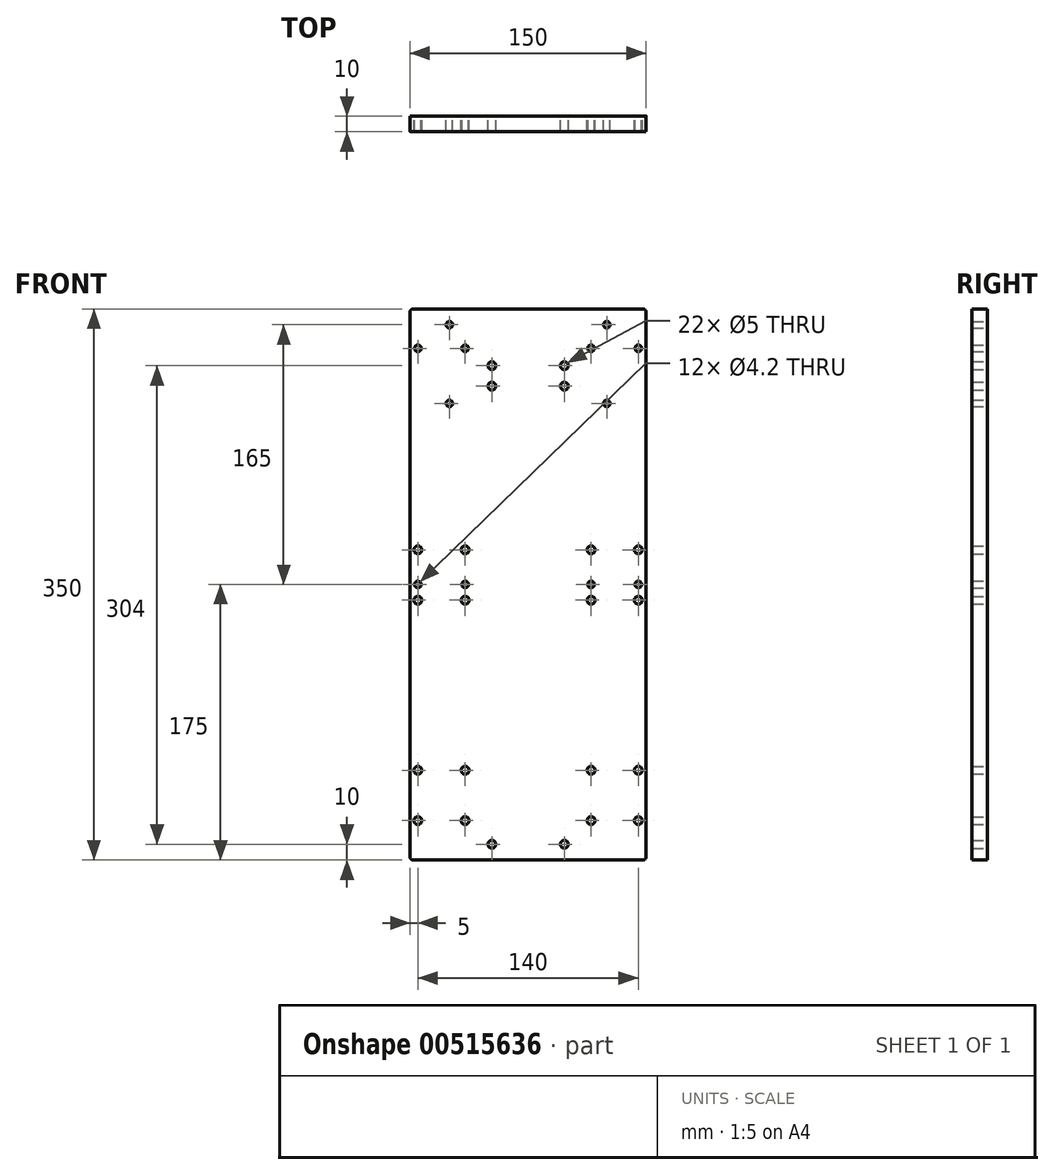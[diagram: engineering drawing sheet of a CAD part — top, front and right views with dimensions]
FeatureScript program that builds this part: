
annotation { "Feature Type Name" : "Feature", "Feature Type Description" : "" }
export const myFeature = defineFeature(function(context is Context, id is Id, definition is map)
    precondition{}
    {
        {
            var Q0;
            Q0=qCreatedBy(makeId("Front.planeOp"),FACE);
            var sketch = newSketch(context, id + "F0", { "sketchPlane" : qUnion([Q0]), "disableImprinting" : false});
            skLineSegment(sketch, "E0.bottom", {"start": v(-73, 175) * mm, "end": v(73, 175) * mm});
            skLineSegment(sketch, "E0.top", {"start": v(-73, -175) * mm, "end": v(73, -175) * mm});
            skLineSegment(sketch, "E0.left", {"start": v(-75, 173) * mm, "end": v(-75, -173) * mm});
            skLineSegment(sketch, "E0.right", {"start": v(75, 173) * mm, "end": v(75, -173) * mm});
            skPoint(sketch, "E0.middle", {"position": v(0, 0) * mm});
            skLineSegment(sketch, "E1", {"start": v(-55, 175) * mm, "end": v(-55, -175) * mm, "construction": true});
            skCircle(sketch, "E2", {"center": v(-70, 0) * mm, "radius": 2.1 * mm});
            skCircle(sketch, "E3.MirrorC", {"center": v(-40, 0) * mm, "radius": 2.1 * mm});
            skCircle(sketch, "E4.MirrorC", {"center": v(40, 0) * mm, "radius": 2.1 * mm});
            skCircle(sketch, "E5.MirrorC", {"center": v(70, 0) * mm, "radius": 2.1 * mm});
            skLineSegment(sketch, "E6", {"start": v(-75, -150) * mm, "end": v(75, -150) * mm, "construction": true});
            skCircle(sketch, "E7", {"center": v(-70, -150) * mm, "radius": 2.5 * mm});
            skCircle(sketch, "E8.MirrorC", {"center": v(-40, -150) * mm, "radius": 2.5 * mm});
            skCircle(sketch, "E9.MirrorC", {"center": v(40, -150) * mm, "radius": 2.5 * mm});
            skCircle(sketch, "E10.MirrorC", {"center": v(70, -150) * mm, "radius": 2.5 * mm});
            skLineSegment(sketch, "E11", {"start": v(-75, -134) * mm, "end": v(-55, -134) * mm, "construction": true});
            skCircle(sketch, "E12.MirrorC", {"center": v(-70, -118) * mm, "radius": 2.5 * mm});
            skCircle(sketch, "E13.MirrorC", {"center": v(-40, -118) * mm, "radius": 2.5 * mm});
            skLineSegment(sketch, "E14", {"start": v(-55, -64) * mm, "end": v(-75, -64) * mm, "construction": true});
            skCircle(sketch, "E15.MirrorC", {"center": v(-70, -10) * mm, "radius": 2.5 * mm});
            skCircle(sketch, "E16.MirrorC", {"center": v(-40, -10) * mm, "radius": 2.5 * mm});
            skCircle(sketch, "E17.MirrorC", {"center": v(-40, 22) * mm, "radius": 2.5 * mm});
            skCircle(sketch, "E18.MirrorC", {"center": v(-70, 22) * mm, "radius": 2.5 * mm});
            skCircle(sketch, "E19.MirrorC", {"center": v(40, -118) * mm, "radius": 2.5 * mm});
            skCircle(sketch, "E20.MirrorC", {"center": v(70, -118) * mm, "radius": 2.5 * mm});
            skCircle(sketch, "E21.MirrorC", {"center": v(40, 22) * mm, "radius": 2.5 * mm});
            skCircle(sketch, "E22.MirrorC", {"center": v(70, 22) * mm, "radius": 2.5 * mm});
            skCircle(sketch, "E23.MirrorC", {"center": v(70, -10) * mm, "radius": 2.5 * mm});
            skCircle(sketch, "E24.MirrorC", {"center": v(40, -10) * mm, "radius": 2.5 * mm});
            skLineSegment(sketch, "E25", {"start": v(-55, 75) * mm, "end": v(-75, 75) * mm, "construction": true});
            skCircle(sketch, "E26.MirrorC", {"center": v(-70, 150) * mm, "radius": 2.1 * mm});
            skCircle(sketch, "E27.MirrorC", {"center": v(-40, 150) * mm, "radius": 2.1 * mm});
            skCircle(sketch, "E28.MirrorC", {"center": v(40, 150) * mm, "radius": 2.1 * mm});
            skCircle(sketch, "E29.MirrorC", {"center": v(70, 150) * mm, "radius": 2.1 * mm});
            skPoint(sketch, "E30.visualSharp", {"position": v(-75, 175) * mm});
            skArc(sketch, "E30.filletArc", {"start": v(-73, 175) * mm, "mid": v(-74.41, 174.41) * mm, "end": v(-75, 173) * mm});
            skPoint(sketch, "E31.visualSharp", {"position": v(75, 175) * mm});
            skArc(sketch, "E31.filletArc", {"start": v(75, 173) * mm, "mid": v(74.41, 174.41) * mm, "end": v(73, 175) * mm});
            skPoint(sketch, "E32.visualSharp", {"position": v(75, -175) * mm});
            skArc(sketch, "E32.filletArc", {"start": v(73, -175) * mm, "mid": v(74.41, -174.41) * mm, "end": v(75, -173) * mm});
            skPoint(sketch, "E33.visualSharp", {"position": v(-75, -175) * mm});
            skArc(sketch, "E33.filletArc", {"start": v(-75, -173) * mm, "mid": v(-74.41, -174.41) * mm, "end": v(-73, -175) * mm});
            skCircle(sketch, "E34", {"center": v(-23, -165) * mm, "radius": 2.5 * mm});
            skCircle(sketch, "E35.MirrorC", {"center": v(23, -165) * mm, "radius": 2.5 * mm});
            skLineSegment(sketch, "E36", {"start": v(-75, -155) * mm, "end": v(75, -155) * mm, "construction": true});
            skLineSegment(sketch, "E37", {"start": v(-75, 120) * mm, "end": v(75, 120) * mm, "construction": true});
            skCircle(sketch, "E38", {"center": v(-23, 126) * mm, "radius": 2.5 * mm});
            skCircle(sketch, "E39", {"center": v(-23, 139) * mm, "radius": 2.5 * mm});
            skCircle(sketch, "E40.MirrorC", {"center": v(23, 126) * mm, "radius": 2.5 * mm});
            skCircle(sketch, "E41.MirrorC", {"center": v(23, 139) * mm, "radius": 2.5 * mm});
            skCircle(sketch, "E42", {"center": v(-50, 165) * mm, "radius": 2.1 * mm});
            skCircle(sketch, "E43", {"center": v(-50, 115) * mm, "radius": 2.1 * mm});
            skCircle(sketch, "E44.MirrorC", {"center": v(50, 115) * mm, "radius": 2.1 * mm});
            skCircle(sketch, "E45.MirrorC", {"center": v(50, 165) * mm, "radius": 2.1 * mm});
            skSolve(sketch);
        }
        {
            var Q0;
            Q0 = qSketchRegion(id + "F0", true);
            extrude(context, id + "F1", {"entities" : qUnion([Q0]), "flatOperationType" : FlatOperationType.REMOVE, "depth" : 10 * mm, "offsetDistance" : 25 * mm, "domain" : OperationDomain.MODEL});
        }
    });
